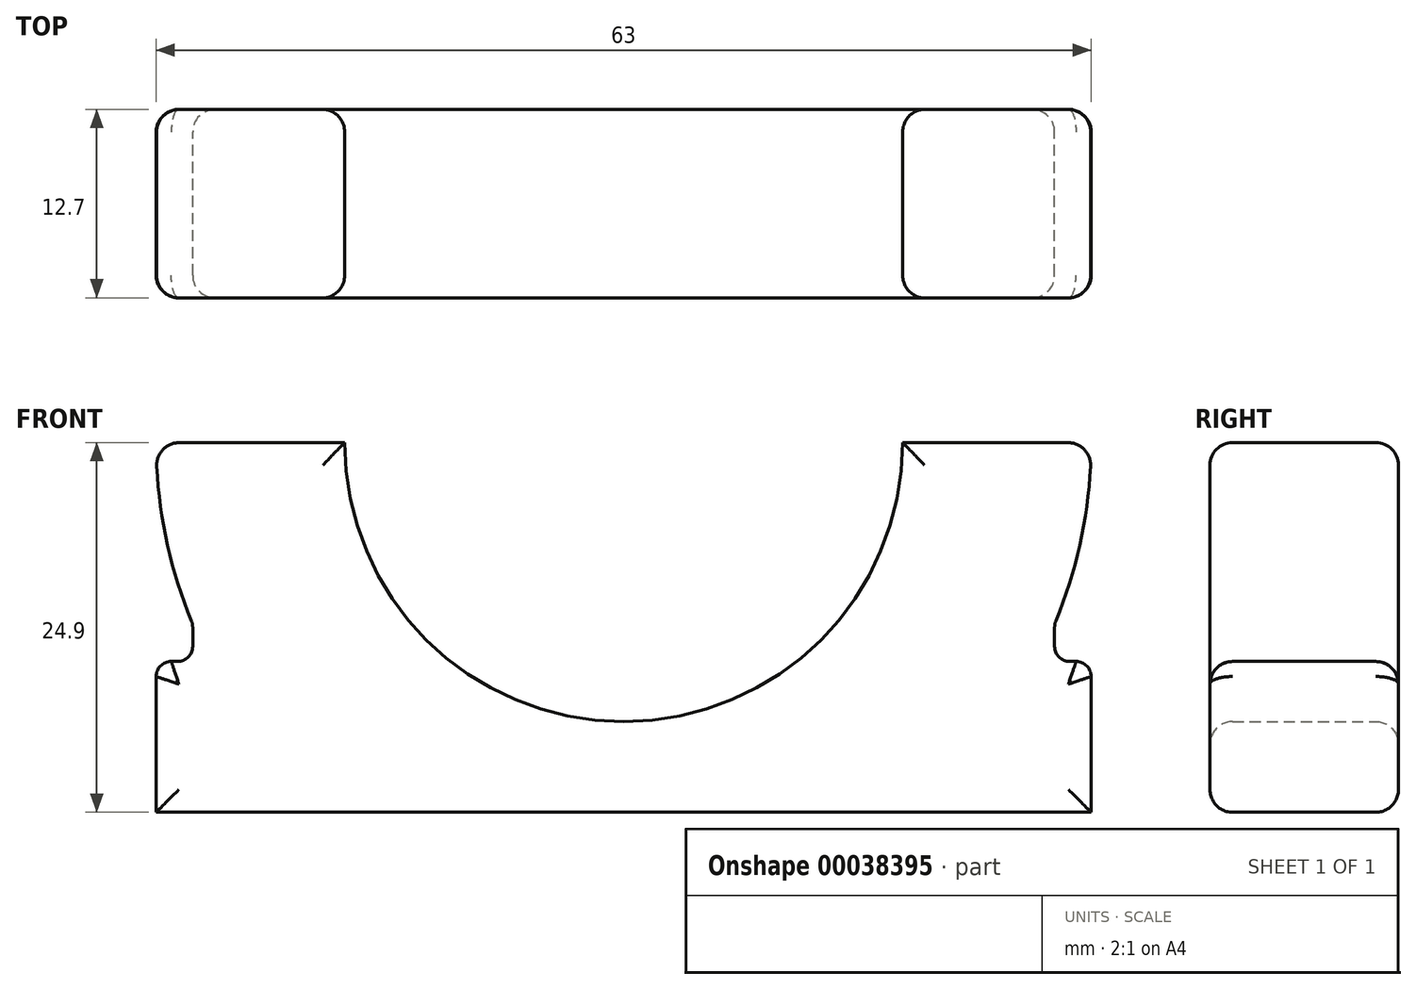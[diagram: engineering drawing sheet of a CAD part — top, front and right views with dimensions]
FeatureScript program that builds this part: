
annotation { "Feature Type Name" : "Feature", "Feature Type Description" : "" }
export const myFeature = defineFeature(function(context is Context, id is Id, definition is map)
    precondition{}
    {
        {
            var Q0;
            Q0=qCreatedBy(makeId("Front.planeOp"),FACE);
            var sketch = newSketch(context, id + "F0", { "sketchPlane" : qUnion([Q0])});
            skCircle(sketch, "E0", {"center": v(0, 0) * mm, "radius": 18.8 * mm, "construction": true});
            skArc(sketch, "E1", {"start": v(-31.5, 0) * mm, "mid": v(-30.87, -6.23) * mm, "end": v(-29.04, -12.2) * mm});
            skLineSegment(sketch, "E2", {"start": v(-45.79, 0) * mm, "end": v(50.26, 0) * mm, "construction": true});
            skArc(sketch, "E3", {"start": v(-18.8, 0) * mm, "mid": v(0, -18.8) * mm, "end": v(18.8, 0) * mm});
            skLineSegment(sketch, "E4", {"start": v(-31.5, 0) * mm, "end": v(-18.8, 0) * mm});
            skLineSegment(sketch, "E5", {"start": v(18.8, 0) * mm, "end": v(31.5, 0) * mm});
            skLineSegment(sketch, "E6", {"start": v(0, 0) * mm, "end": v(0, -48.51) * mm, "construction": true});
            skLineSegment(sketch, "E7.rect.bottom", {"start": v(31.5, -24.9) * mm, "end": v(-31.5, -24.9) * mm});
            skLineSegment(sketch, "E7.rect.top", {"start": v(31.5, -14.74) * mm, "end": v(29.04, -14.74) * mm});
            skLineSegment(sketch, "E7.rect.left", {"start": v(31.5, -24.9) * mm, "end": v(31.5, -14.74) * mm});
            skLineSegment(sketch, "E7.rect.right", {"start": v(-31.5, -24.9) * mm, "end": v(-31.5, -14.74) * mm});
            skPoint(sketch, "E7.rect.middle", {"position": v(0, -19.82) * mm});
            skLineSegment(sketch, "E8", {"start": v(-29.04, -12.2) * mm, "end": v(-29.04, -14.74) * mm});
            skLineSegment(sketch, "E9.MirrorCS", {"start": v(29.04, -12.2) * mm, "end": v(29.04, -14.74) * mm});
            skArc(sketch, "E10.trimOffspring", {"start": v(29.04, -12.2) * mm, "mid": v(30.87, -6.23) * mm, "end": v(31.5, 0) * mm});
            skLineSegment(sketch, "E11.trimOffspring", {"start": v(-29.04, -14.74) * mm, "end": v(-31.5, -14.74) * mm});
            skSolve(sketch);
        }
        {
            var Q0;
            Q0=makeQuery(id+"F0.imprint","IMPRINT",FACE,{"disambiguationData":[TD([[makeQuery(id+"F0.imprint","IMPRINT",EDGE,{"derivedFrom":sQuery(id+"F0.wireOp",EDGE,"E1")}),1.0]])]});
            extrude(context, id + "F1", {"entities" : qUnion([Q0]), "depth" : 12.7 * mm});
        }
        {
            var Q0;
            Q0=makeQuery(id+"F1.opExtrude","SWEPT_EDGE",EDGE,{"disambiguationData":[OSD([sQuery(id+"F0.wireOp",EDGE,"E7.rect.top"),sQuery(id+"F0.wireOp",EDGE,"E9.MirrorCS")])]});
            var Q1;
            Q1=makeQuery(id+"F1.opExtrude","SWEPT_EDGE",EDGE,{"disambiguationData":[OSD([sQuery(id+"F0.wireOp",EDGE,"E7.rect.top"),sQuery(id+"F0.wireOp",EDGE,"E7.rect.left")])]});
            var Q2;
            Q2=makeQuery(id+"F1.opExtrude","SWEPT_EDGE",EDGE,{"disambiguationData":[OSD([sQuery(id+"F0.wireOp",EDGE,"E9.MirrorCS"),sQuery(id+"F0.wireOp",EDGE,"E10.trimOffspring")])]});
            var Q3;
            Q3=makeQuery(id+"F1.opExtrude","SWEPT_EDGE",EDGE,{"disambiguationData":[OSD([sQuery(id+"F0.wireOp",EDGE,"E7.rect.right"),sQuery(id+"F0.wireOp",EDGE,"E11.trimOffspring")])]});
            var Q4;
            Q4=makeQuery(id+"F1.opExtrude","SWEPT_EDGE",EDGE,{"disambiguationData":[OSD([sQuery(id+"F0.wireOp",EDGE,"E8"),sQuery(id+"F0.wireOp",EDGE,"E11.trimOffspring")])]});
            var Q5;
            Q5=makeQuery(id+"F1.opExtrude","SWEPT_EDGE",EDGE,{"disambiguationData":[OSD([sQuery(id+"F0.wireOp",EDGE,"E1"),sQuery(id+"F0.wireOp",EDGE,"E8")])]});
            fillet(context, id + "F2", {"entities" : qUnion([Q0, Q1, Q2, Q3, Q4, Q5]), "radius" : 1.02 * mm, "tangentPropagation" : true, "allowEdgeOverflow" : false});
        }
        {
            var Q0;
            Q0=makeQuery(id+"F1.opExtrude","CAP_FACE",FACE,{"disambiguationData":[OSD([sQuery(id+"F0.wireOp",EDGE,"E1"),sQuery(id+"F0.wireOp",EDGE,"E3"),sQuery(id+"F0.wireOp",EDGE,"E4"),sQuery(id+"F0.wireOp",EDGE,"E5"),sQuery(id+"F0.wireOp",EDGE,"E7.rect.bottom"),sQuery(id+"F0.wireOp",EDGE,"E7.rect.top"),sQuery(id+"F0.wireOp",EDGE,"E7.rect.left"),sQuery(id+"F0.wireOp",EDGE,"E7.rect.right"),sQuery(id+"F0.wireOp",EDGE,"E8"),sQuery(id+"F0.wireOp",EDGE,"E9.MirrorCS"),sQuery(id+"F0.wireOp",EDGE,"E10.trimOffspring"),sQuery(id+"F0.wireOp",EDGE,"E11.trimOffspring")])],"isStart":true});
            var Q1;
            Q1=makeQuery(id+"F1.opExtrude","CAP_FACE",FACE,{"disambiguationData":[OSD([sQuery(id+"F0.wireOp",EDGE,"E1"),sQuery(id+"F0.wireOp",EDGE,"E3"),sQuery(id+"F0.wireOp",EDGE,"E4"),sQuery(id+"F0.wireOp",EDGE,"E5"),sQuery(id+"F0.wireOp",EDGE,"E7.rect.bottom"),sQuery(id+"F0.wireOp",EDGE,"E7.rect.top"),sQuery(id+"F0.wireOp",EDGE,"E7.rect.left"),sQuery(id+"F0.wireOp",EDGE,"E7.rect.right"),sQuery(id+"F0.wireOp",EDGE,"E8"),sQuery(id+"F0.wireOp",EDGE,"E9.MirrorCS"),sQuery(id+"F0.wireOp",EDGE,"E10.trimOffspring"),sQuery(id+"F0.wireOp",EDGE,"E11.trimOffspring")])],"isStart":false});
            var Q2;
            Q2=makeQuery(id+"F1.opExtrude","SWEPT_EDGE",EDGE,{"disambiguationData":[OSD([sQuery(id+"F0.wireOp",EDGE,"E5"),sQuery(id+"F0.wireOp",EDGE,"E10.trimOffspring")])]});
            var Q3;
            Q3=makeQuery(id+"F1.opExtrude","SWEPT_EDGE",EDGE,{"disambiguationData":[OSD([sQuery(id+"F0.wireOp",EDGE,"E1"),sQuery(id+"F0.wireOp",EDGE,"E4")])]});
            fillet(context, id + "F3", {"entities" : qUnion([Q0, Q1, Q2, Q3]), "radius" : 1.52 * mm, "tangentPropagation" : true, "allowEdgeOverflow" : false});
        }
    });
